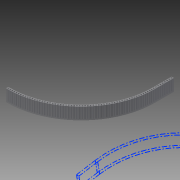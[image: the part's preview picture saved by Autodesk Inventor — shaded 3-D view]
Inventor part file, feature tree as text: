
AUTODESK INVENTOR PART (.ipt)
format: ipt  version: 2013 (Build 170138000, 138)  size: 259,584 bytes
history: native  units: in
note: dims shown in document units (in); Inventor stores cm internally (conversion verified against a paired STEP export)
features: extrude x3, sketch x3
ambient origin geometry x8: Origin, YZ Plane, XZ Plane, XY Plane, X Axis, Y Axis, Z Axis, Center Point
bodies: Solid1 (feature_tree)
feature tree (6):
  extrude  "Extrusion1"  Depth=28.0in
  extrude  "Extrusion5"  Depth=2.5in TaperAngle=0.0deg
  extrude  "Extrusion9"  Depth=4.5in
  sketch  "Sketch1"  dims[d0=8.0in d2=28.0in]
  sketch  "Sketch5"  dims[d5=11.0in d7=2.5in d8=0.0in]
  sketch  "Sketch11"  dims[d46=0.925in d47=0.425in d67=4.5in d89=0.925in d93=0.5in d94=0.266in d95=0.25in d96=0.266in d97=0.266in d98=0.25in d99=0.25in d100=0.25in d101=0.25in d102=0.25in d103=4.0in d104=25.0in d105=4.0in d106=3.1496in d108=0.4688in d109=0.3937in d111=1.0in d113=3.937in d115=0.375in d116=0.3937in d118=1.0in d120=23.622in d122=90.0deg d124=2.5in d125=0.0in d142=3.75in d143=100.0in d144=0.0in]
